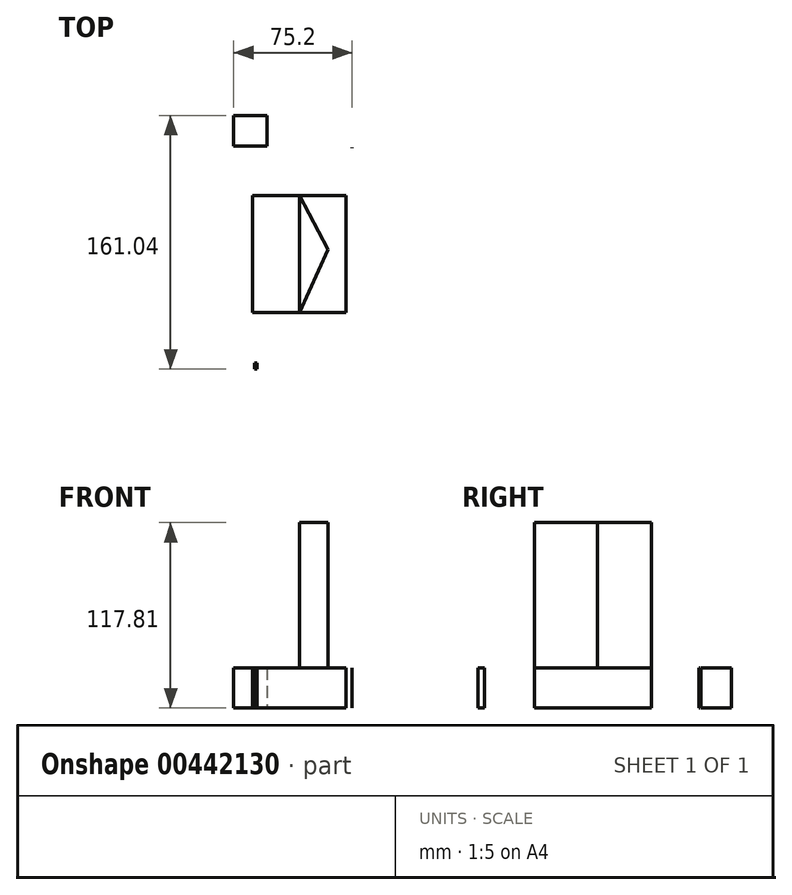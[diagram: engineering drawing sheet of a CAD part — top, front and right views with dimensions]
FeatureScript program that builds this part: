
annotation { "Feature Type Name" : "Feature", "Feature Type Description" : "" }
export const myFeature = defineFeature(function(context is Context, id is Id, definition is map)
    precondition{}
    {
        {
            var Q0;
            Q0=qCreatedBy(makeId("Top.planeOp"),FACE);
            var sketch = newSketch(context, id + "F0", { "sketchPlane" : qUnion([Q0])});
            skLineSegment(sketch, "E0.bottom", {"start": v(74.97, 0) * mm, "end": v(0, 0) * mm});
            skLineSegment(sketch, "E0.top", {"start": v(74.97, 0) * mm, "end": v(0, 0) * mm});
            skLineSegment(sketch, "E0.left", {"start": v(74.97, 0) * mm, "end": v(74.97, 0) * mm});
            skLineSegment(sketch, "E0.right", {"start": v(0, 0) * mm, "end": v(0, 0) * mm});
            skLineSegment(sketch, "E1.top", {"start": v(74.97, -76.6) * mm, "end": v(74.97, -76.6) * mm});
            skLineSegment(sketch, "E1.left", {"start": v(74.97, 0) * mm, "end": v(74.97, -76.6) * mm});
            skLineSegment(sketch, "E1.right", {"start": v(74.97, 0) * mm, "end": v(74.97, -76.6) * mm});
            skLineSegment(sketch, "E2.bottom", {"start": v(13.27, -71.92) * mm, "end": v(14.79, -71.92) * mm});
            skLineSegment(sketch, "E2.top", {"start": v(13.27, -75.87) * mm, "end": v(14.79, -75.87) * mm});
            skLineSegment(sketch, "E2.left", {"start": v(13.27, -71.92) * mm, "end": v(13.27, -75.87) * mm});
            skLineSegment(sketch, "E2.right", {"start": v(14.79, -71.92) * mm, "end": v(14.79, -75.87) * mm});
            skLineSegment(sketch, "E3.top", {"start": v(74.97, 64.88) * mm, "end": v(74.97, 64.88) * mm});
            skLineSegment(sketch, "E3.left", {"start": v(74.97, 0) * mm, "end": v(74.97, 64.88) * mm});
            skLineSegment(sketch, "E3.right", {"start": v(74.97, 0) * mm, "end": v(74.97, 64.88) * mm});
            skLineSegment(sketch, "E4.bottom", {"start": v(0, 63.84) * mm, "end": v(0, 63.84) * mm});
            skLineSegment(sketch, "E4.top", {"start": v(0, 65.73) * mm, "end": v(0, 65.73) * mm});
            skLineSegment(sketch, "E4.left", {"start": v(0, 63.84) * mm, "end": v(0, 65.73) * mm});
            skLineSegment(sketch, "E4.right", {"start": v(0, 63.84) * mm, "end": v(0, 65.73) * mm});
            skLineSegment(sketch, "E5.bottom", {"start": v(75.2, 64.36) * mm, "end": v(74.97, 64.36) * mm});
            skLineSegment(sketch, "E5.top", {"start": v(75.2, 64.88) * mm, "end": v(74.97, 64.88) * mm});
            skLineSegment(sketch, "E5.left", {"start": v(75.2, 64.36) * mm, "end": v(75.2, 64.88) * mm});
            skLineSegment(sketch, "E5.right", {"start": v(74.97, 64.36) * mm, "end": v(74.97, 64.88) * mm});
            skLineSegment(sketch, "E6.bottom", {"start": v(0, 65.73) * mm, "end": v(21.23, 65.73) * mm});
            skLineSegment(sketch, "E6.top", {"start": v(0, 85.17) * mm, "end": v(21.23, 85.17) * mm});
            skLineSegment(sketch, "E6.left", {"start": v(0, 65.73) * mm, "end": v(0, 85.17) * mm});
            skLineSegment(sketch, "E6.right", {"start": v(21.23, 65.73) * mm, "end": v(21.23, 85.17) * mm});
            skLineSegment(sketch, "E7.bottom", {"start": v(11.85, 34.36) * mm, "end": v(71.42, 34.36) * mm});
            skLineSegment(sketch, "E7.top", {"start": v(11.85, -39.98) * mm, "end": v(71.42, -39.98) * mm});
            skLineSegment(sketch, "E7.left", {"start": v(11.85, 34.36) * mm, "end": v(11.85, -39.98) * mm});
            skLineSegment(sketch, "E7.right", {"start": v(71.42, 34.36) * mm, "end": v(71.42, -39.98) * mm});
            skSolve(sketch);
        }
        {
            var Q0;
            Q0 = qSketchRegion(id + "F0", true);
            var Q1;
            {var subQ5=sQuery(id+"F0.wireOp",EDGE,"E7.top");Q1=makeQuery(id+"F0.imprint","IMPRINT",FACE,{"disambiguationData":[TD([[makeQuery(id+"F0.imprint","IMPRINT",EDGE,{"derivedFrom":subQ5}),1.0]])]});}
            extrude(context, id + "F1", {"entities" : qUnion([Q0, Q1]), "depth" : 25.4 * mm});
        }
        {
            var Q0;
            Q0=makeQuery(id+"F1.opExtrude","CAP_FACE",FACE,{"disambiguationData":[OSD([sQuery(id+"F0.wireOp",EDGE,"E7.bottom"),sQuery(id+"F0.wireOp",EDGE,"E7.top"),sQuery(id+"F0.wireOp",EDGE,"E7.left"),sQuery(id+"F0.wireOp",EDGE,"E7.right")])],"isStart":false});
            var sketch = newSketch(context, id + "F2", { "sketchPlane" : qUnion([Q0])});
            skLineSegment(sketch, "E8", {"start": v(41.64, -39.98) * mm, "end": v(41.64, 34.36) * mm});
            skLineSegment(sketch, "E9", {"start": v(41.64, 34.36) * mm, "end": v(59.78, 0) * mm});
            skLineSegment(sketch, "E10", {"start": v(59.78, 0) * mm, "end": v(41.64, -39.98) * mm});
            skSolve(sketch);
        }
        {
            var Q0;
            Q0 = qSketchRegion(id + "F2", true);
            extrude(context, id + "F3", {"entities" : qUnion([Q0]), "operationType" : NewBodyOperationType.ADD, "depth" : 92.4 * mm});
        }
    });
